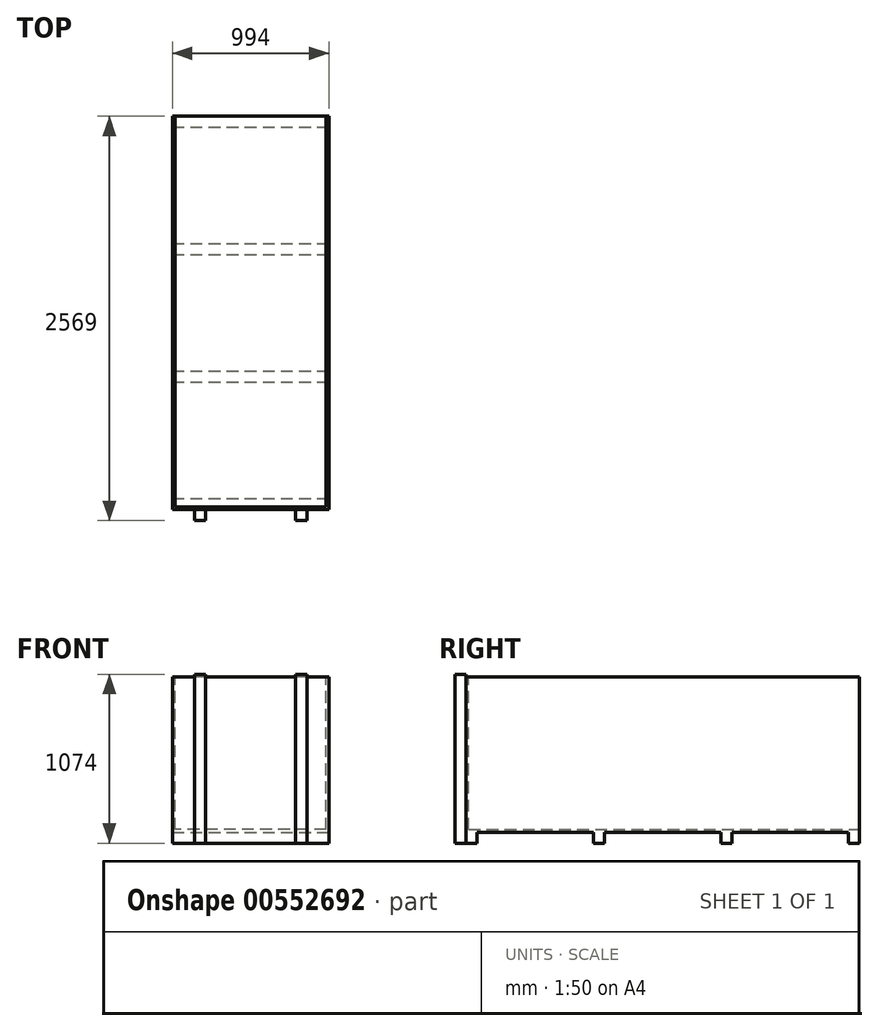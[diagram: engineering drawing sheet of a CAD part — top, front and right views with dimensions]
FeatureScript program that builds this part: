
annotation { "Feature Type Name" : "Feature", "Feature Type Description" : "" }
export const myFeature = defineFeature(function(context is Context, id is Id, definition is map)
    precondition{}
    {
        {
            var Q0;
            Q0=qCreatedBy(makeId("Top.planeOp"),FACE);
            var sketch = newSketch(context, id + "F0", { "sketchPlane" : qUnion([Q0])});
            skLineSegment(sketch, "E0.bottom", {"start": v(497, 1249.5) * mm, "end": v(-497, 1249.5) * mm});
            skLineSegment(sketch, "E0.top", {"start": v(497, -1249.5) * mm, "end": v(-497, -1249.5) * mm});
            skLineSegment(sketch, "E0.left", {"start": v(497, 1249.5) * mm, "end": v(497, -1249.5) * mm});
            skLineSegment(sketch, "E0.right", {"start": v(-497, 1249.5) * mm, "end": v(-497, -1249.5) * mm});
            skPoint(sketch, "E0.middle", {"position": v(0, 0) * mm});
            skSolve(sketch);
        }
        {
            var Q0;
            Q0 = qSketchRegion(id + "F0", true);
            extrude(context, id + "F1", {"entities" : qUnion([Q0]), "oppositeDirection" : true, "depth" : (970 + 17) * mm, "offsetDistance" : 25 * mm});
        }
        {
            var Q0;
            Q0=qCreatedBy(makeId("Top.planeOp"),FACE);
            var sketch = newSketch(context, id + "F2", { "sketchPlane" : qUnion([Q0])});
            skLineSegment(sketch, "E1.bottom", {"start": v(480, -1232.5) * mm, "end": v(-480, -1232.5) * mm});
            skLineSegment(sketch, "E1.top", {"start": v(480, 1249.5) * mm, "end": v(-480, 1249.5) * mm});
            skLineSegment(sketch, "E1.left", {"start": v(480, -1232.5) * mm, "end": v(480, 1249.5) * mm});
            skLineSegment(sketch, "E1.right", {"start": v(-480, -1232.5) * mm, "end": v(-480, 1249.5) * mm});
            skSolve(sketch);
        }
        {
            var Q0;
            Q0 = qSketchRegion(id + "F2", true);
            extrude(context, id + "F3", {"entities" : qUnion([Q0]), "operationType" : NewBodyOperationType.REMOVE, "oppositeDirection" : true, "depth" : 970 * mm, "offsetDistance" : 25 * mm});
        }
        {
            var Q0;
            Q0=qCreatedBy(makeId("Top.planeOp"),FACE);
            cPlane(context, id + "F4", {"entities" : qUnion([Q0]), "cplaneType" : CPlaneType.OFFSET, "offset" : 17 * mm, "width" : 150 * mm, "height" : 150 * mm});
        }
        {
            var Q0;
            Q0=qCreatedBy(id+"F4.planeOp",FACE);
            var sketch = newSketch(context, id + "F5", { "sketchPlane" : qUnion([Q0])});
            skLineSegment(sketch, "E2.bottom", {"start": v(-357, -1319.5) * mm, "end": v(-287, -1319.5) * mm});
            skLineSegment(sketch, "E2.top", {"start": v(-357, -1249.5) * mm, "end": v(-287, -1249.5) * mm});
            skLineSegment(sketch, "E2.left", {"start": v(-357, -1319.5) * mm, "end": v(-357, -1249.5) * mm});
            skLineSegment(sketch, "E2.right", {"start": v(-287, -1319.5) * mm, "end": v(-287, -1249.5) * mm});
            skLineSegment(sketch, "E3.bottom", {"start": v(287, -1319.5) * mm, "end": v(357, -1319.5) * mm});
            skLineSegment(sketch, "E3.top", {"start": v(287, -1249.5) * mm, "end": v(357, -1249.5) * mm});
            skLineSegment(sketch, "E3.left", {"start": v(287, -1319.5) * mm, "end": v(287, -1249.5) * mm});
            skLineSegment(sketch, "E3.right", {"start": v(357, -1319.5) * mm, "end": v(357, -1249.5) * mm});
            skSolve(sketch);
        }
        {
            var Q0;
            Q0 = qSketchRegion(id + "F5", true);
            extrude(context, id + "F6", {"entities" : qUnion([Q0]), "oppositeDirection" : true, "depth" : (970 + 34 + (35 * 2)) * mm, "offsetDistance" : 25 * mm});
        }
        {
            var Q0;
            Q0=makeQuery(id+"F1.opExtrude","CAP_FACE",FACE,{"disambiguationData":[OSD([sQuery(id+"F0.wireOp",EDGE,"E0.bottom"),sQuery(id+"F0.wireOp",EDGE,"E0.top"),sQuery(id+"F0.wireOp",EDGE,"E0.left"),sQuery(id+"F0.wireOp",EDGE,"E0.right")])],"isStart":false});
            var sketch = newSketch(context, id + "F7", { "sketchPlane" : qUnion([Q0])});
            skLineSegment(sketch, "E4.bottom", {"start": v(-497, -1249.5) * mm, "end": v(497, -1249.5) * mm});
            skLineSegment(sketch, "E4.top", {"start": v(-497, -1179.5) * mm, "end": v(497, -1179.5) * mm});
            skLineSegment(sketch, "E4.left", {"start": v(-497, -1249.5) * mm, "end": v(-497, -1179.5) * mm});
            skLineSegment(sketch, "E4.right", {"start": v(497, -1249.5) * mm, "end": v(497, -1179.5) * mm});
            skLineSegment(sketch, "E5.bottom", {"start": v(-497, -439.5) * mm, "end": v(497, -439.5) * mm});
            skLineSegment(sketch, "E5.top", {"start": v(-497, -369.5) * mm, "end": v(497, -369.5) * mm});
            skLineSegment(sketch, "E5.left", {"start": v(-497, -439.5) * mm, "end": v(-497, -369.5) * mm});
            skLineSegment(sketch, "E5.right", {"start": v(497, -439.5) * mm, "end": v(497, -369.5) * mm});
            skLineSegment(sketch, "E6.bottom", {"start": v(-497, 1179.5) * mm, "end": v(497, 1179.5) * mm});
            skLineSegment(sketch, "E6.top", {"start": v(-497, 1249.5) * mm, "end": v(497, 1249.5) * mm});
            skLineSegment(sketch, "E6.left", {"start": v(-497, 1179.5) * mm, "end": v(-497, 1249.5) * mm});
            skLineSegment(sketch, "E6.right", {"start": v(497, 1179.5) * mm, "end": v(497, 1249.5) * mm});
            skLineSegment(sketch, "E7.bottom", {"start": v(-497, 369.5) * mm, "end": v(497, 369.5) * mm});
            skLineSegment(sketch, "E7.top", {"start": v(-497, 439.5) * mm, "end": v(497, 439.5) * mm});
            skLineSegment(sketch, "E7.left", {"start": v(-497, 369.5) * mm, "end": v(-497, 439.5) * mm});
            skLineSegment(sketch, "E7.right", {"start": v(497, 369.5) * mm, "end": v(497, 439.5) * mm});
            skSolve(sketch);
        }
        {
            var Q0;
            Q0 = qSketchRegion(id + "F7", true);
            extrude(context, id + "F8", {"entities" : qUnion([Q0]), "operationType" : NewBodyOperationType.ADD, "depth" : 70 * mm, "offsetDistance" : 25 * mm});
        }
    });
